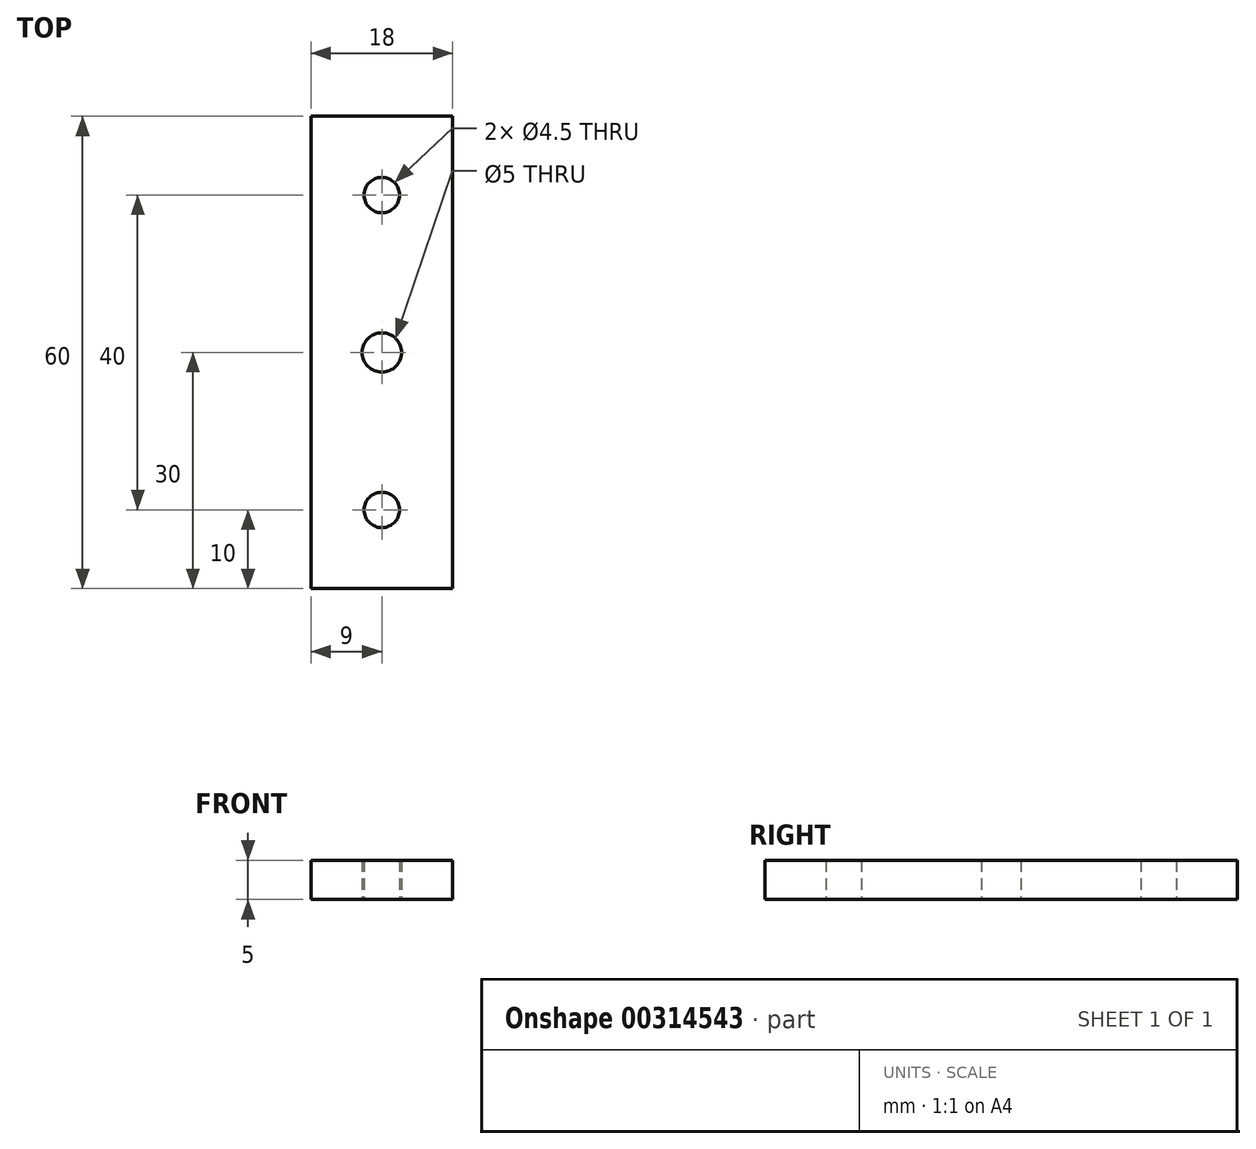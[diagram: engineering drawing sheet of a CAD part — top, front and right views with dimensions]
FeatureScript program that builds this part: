
annotation { "Feature Type Name" : "Feature", "Feature Type Description" : "" }
export const myFeature = defineFeature(function(context is Context, id is Id, definition is map)
    precondition{}
    {
        {
            var Q0;
            Q0=qCreatedBy(makeId("Top.planeOp"),FACE);
            var sketch = newSketch(context, id + "F0", { "sketchPlane" : qUnion([Q0])});
            skLineSegment(sketch, "E0.bottom", {"start": v(-9, -30) * mm, "end": v(9, -30) * mm});
            skLineSegment(sketch, "E0.top", {"start": v(-9, 30) * mm, "end": v(9, 30) * mm});
            skLineSegment(sketch, "E0.left", {"start": v(-9, -30) * mm, "end": v(-9, 30) * mm});
            skLineSegment(sketch, "E0.right", {"start": v(9, -30) * mm, "end": v(9, 30) * mm});
            skPoint(sketch, "E0.middle", {"position": v(0, 0) * mm});
            skCircle(sketch, "E1", {"center": v(0, 0) * mm, "radius": 2.5 * mm});
            skCircle(sketch, "E2", {"center": v(0, 20) * mm, "radius": 2.25 * mm});
            skCircle(sketch, "E3.MirrorC", {"center": v(0, -20) * mm, "radius": 2.25 * mm});
            skSolve(sketch);
        }
        {
            var Q0;
            Q0 = qSketchRegion(id + "F0", true);
            extrude(context, id + "F1", {"entities" : qUnion([Q0]), "depth" : 5 * mm});
        }
    });
